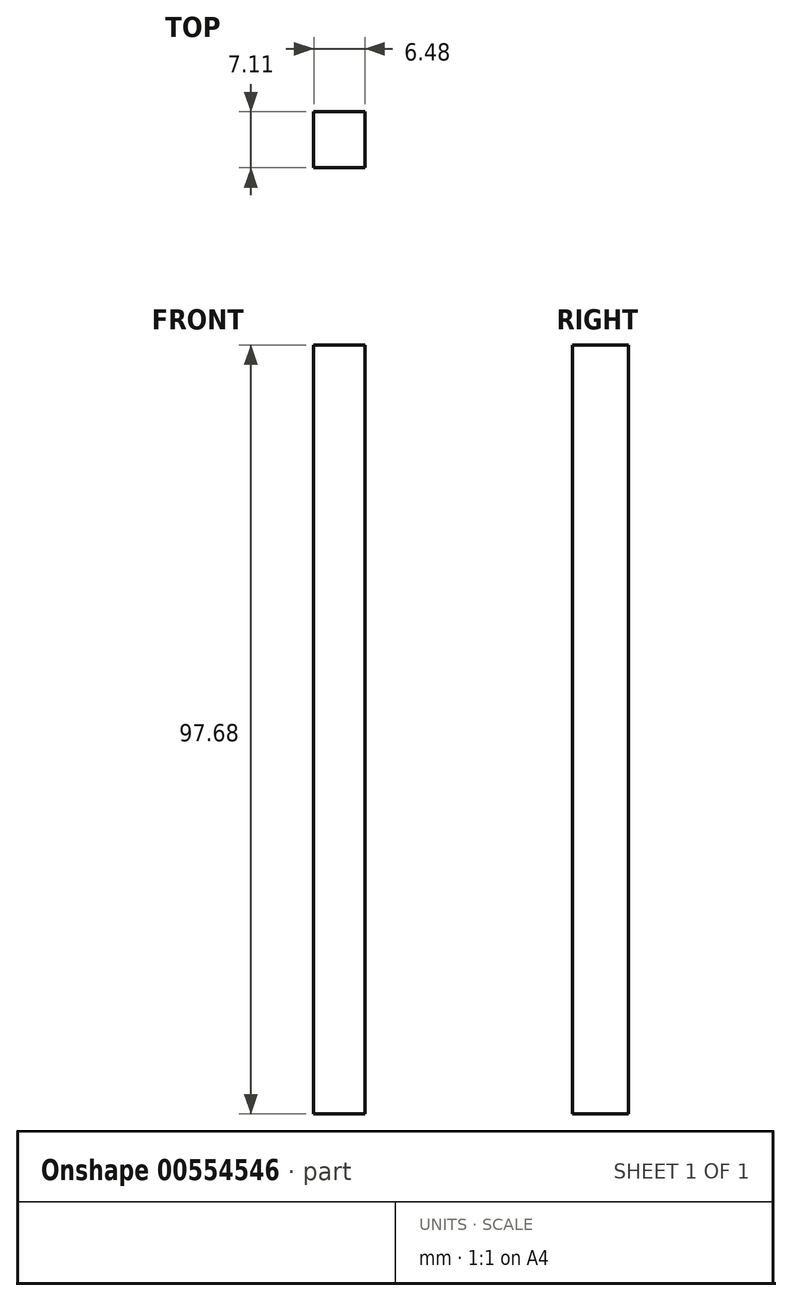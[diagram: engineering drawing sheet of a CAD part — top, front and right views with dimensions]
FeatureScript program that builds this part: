
annotation { "Feature Type Name" : "Feature", "Feature Type Description" : "" }
export const myFeature = defineFeature(function(context is Context, id is Id, definition is map)
    precondition{}
    {
        {
            var Q0;
            Q0=qCreatedBy(makeId("Front.planeOp"),FACE);
            var sketch = newSketch(context, id + "F0", { "sketchPlane" : qUnion([Q0])});
            skLineSegment(sketch, "E0", {"start": v(0, 7.6) * mm, "end": v(0, 60.01) * mm});
            skLineSegment(sketch, "E1", {"start": v(0, 60.01) * mm, "end": v(-6.48, 60.01) * mm});
            skLineSegment(sketch, "E2", {"start": v(-6.48, 60.01) * mm, "end": v(-6.48, -37.67) * mm});
            skLineSegment(sketch, "E3", {"start": v(-6.48, -37.67) * mm, "end": v(0, -37.67) * mm});
            skLineSegment(sketch, "E4", {"start": v(0, -37.67) * mm, "end": v(0, 7.6) * mm});
            skSolve(sketch);
        }
        {
            var Q0;
            Q0 = qSketchRegion(id + "F0", true);
            extrude(context, id + "F1", {"entities" : qUnion([Q0]), "depth" : 7.11 * mm, "offsetDistance" : 25.4 * mm});
        }
    });
